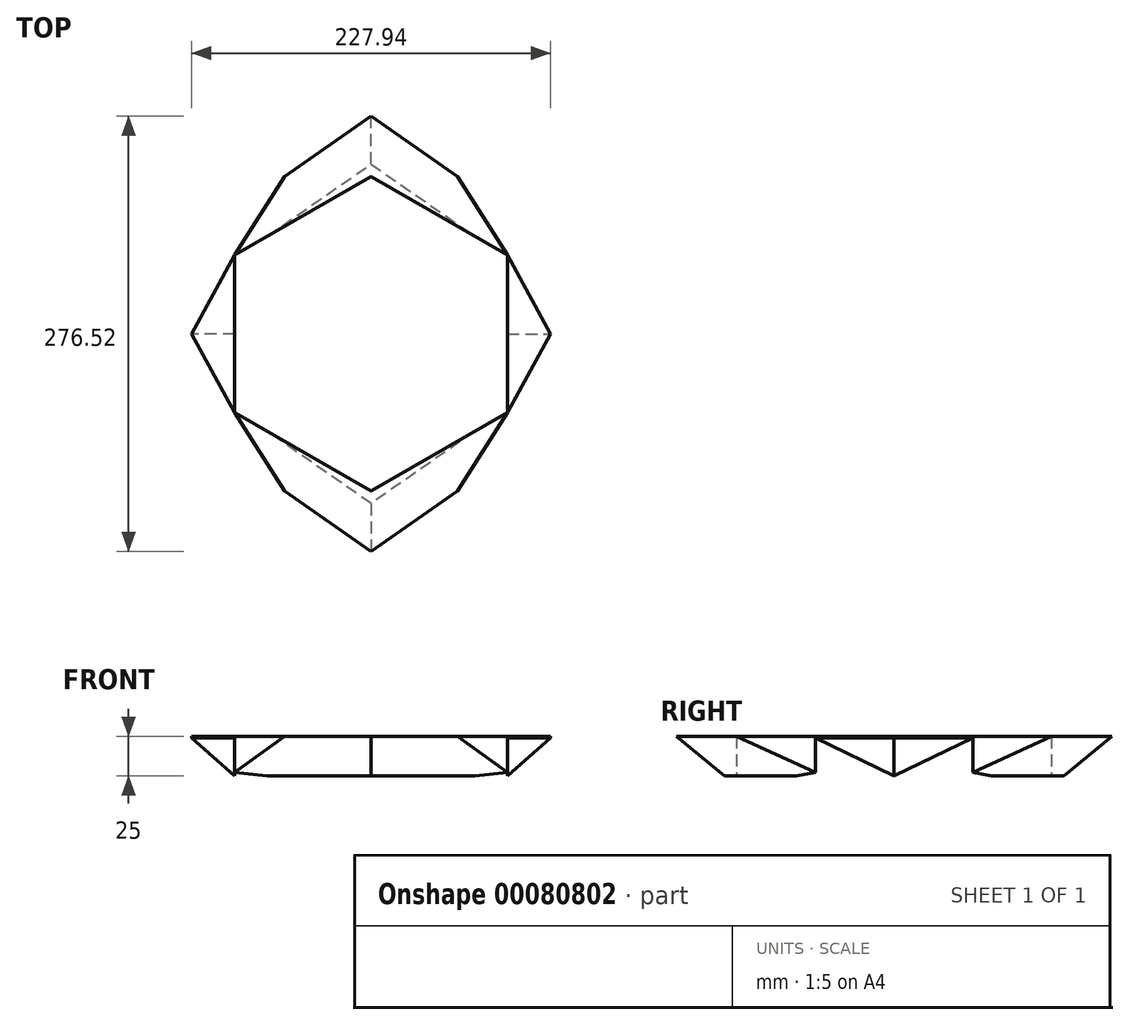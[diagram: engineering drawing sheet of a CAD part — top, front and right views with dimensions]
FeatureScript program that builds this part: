
annotation { "Feature Type Name" : "Feature", "Feature Type Description" : "" }
export const myFeature = defineFeature(function(context is Context, id is Id, definition is map)
    precondition{}
    {
        {
            var Q0;
            Q0=qCreatedBy(makeId("Top.planeOp"),FACE);
            var sketch = newSketch(context, id + "F0", { "sketchPlane" : qUnion([Q0])});
            skLineSegment(sketch, "E0.0", {"start": v(86.6, -50) * mm, "end": v(0, -100) * mm});
            skLineSegment(sketch, "E0.1", {"start": v(0, -100) * mm, "end": v(-86.6, -50) * mm});
            skLineSegment(sketch, "E0.2", {"start": v(-86.6, -50) * mm, "end": v(-86.6, 50) * mm});
            skLineSegment(sketch, "E0.3", {"start": v(-86.6, 50) * mm, "end": v(0, 100) * mm});
            skLineSegment(sketch, "E0.4", {"start": v(0, 100) * mm, "end": v(86.6, 50) * mm});
            skLineSegment(sketch, "E0.5", {"start": v(86.6, 50) * mm, "end": v(86.6, -50) * mm});
            skPoint(sketch, "E0.0.midPoint", {"position": v(43.3, -75) * mm});
            skLineSegment(sketch, "E1", {"start": v(0, 100) * mm, "end": v(-55, 100) * mm});
            skLineSegment(sketch, "E2", {"start": v(-55, 100) * mm, "end": v(-86.6, 50) * mm});
            skLineSegment(sketch, "E3", {"start": v(0, 100) * mm, "end": v(55, 100) * mm});
            skLineSegment(sketch, "E4", {"start": v(55, 100) * mm, "end": v(86.6, 50) * mm});
            skLineSegment(sketch, "E5", {"start": v(-55, 100) * mm, "end": v(0, 138.26) * mm});
            skLineSegment(sketch, "E6", {"start": v(0, 138.26) * mm, "end": v(55, 100) * mm});
            skLineSegment(sketch, "E7", {"start": v(-86.6, -50) * mm, "end": v(-113.97, 0) * mm});
            skLineSegment(sketch, "E8", {"start": v(-113.97, 0) * mm, "end": v(-86.6, 50) * mm});
            skLineSegment(sketch, "E9", {"start": v(86.6, -50) * mm, "end": v(113.97, 0) * mm});
            skLineSegment(sketch, "E10", {"start": v(113.97, 0) * mm, "end": v(86.6, 50) * mm});
            skLineSegment(sketch, "E11.MirrorCS", {"start": v(-55, -100) * mm, "end": v(-86.6, -50) * mm});
            skLineSegment(sketch, "E12.MirrorCS", {"start": v(55, -100) * mm, "end": v(86.6, -50) * mm});
            skLineSegment(sketch, "E13.MirrorCS", {"start": v(0, -100) * mm, "end": v(55, -100) * mm});
            skLineSegment(sketch, "E14.MirrorCS", {"start": v(0, -100) * mm, "end": v(-55, -100) * mm});
            skLineSegment(sketch, "E15.MirrorCS", {"start": v(0, -138.26) * mm, "end": v(55, -100) * mm});
            skLineSegment(sketch, "E16.MirrorCS", {"start": v(-55, -100) * mm, "end": v(0, -138.26) * mm});
            skSolve(sketch);
        }
        {
            var Q0;
            Q0=makeQuery(id+"F0.imprint","IMPRINT",FACE,{"disambiguationData":[TD([[makeQuery(id+"F0.imprint","IMPRINT",EDGE,{"derivedFrom":sQuery(id+"F0.wireOp",EDGE,"E0.0")}),-1.0]])]});
            var sketch = newSketch(context, id + "F1", { "sketchPlane" : qUnion([Q0])});
            skSolve(sketch);
        }
        {
            var Q0;
            Q0 = qSketchRegion(id + "F1", true);
            var Q1;
            Q1=makeQuery(id+"F1.imprint","IMPRINT",FACE,{"disambiguationData":[TD([[makeQuery(id+"F1.imprint","IMPRINT",EDGE,{"derivedFrom":makeQuery(id+"F0.imprint","IMPRINT",EDGE,{"derivedFrom":sQuery(id+"F0.wireOp",EDGE,"E0.0")})}),-1.0]])]});
            var Q2;
            Q2=makeQuery(id+"F0.imprint","IMPRINT",FACE,{"disambiguationData":[TD([[makeQuery(id+"F0.imprint","IMPRINT",EDGE,{"derivedFrom":sQuery(id+"F0.wireOp",EDGE,"E0.4")}),1.0]])]});
            var Q3;
            Q3=makeQuery(id+"F0.imprint","IMPRINT",FACE,{"disambiguationData":[TD([[makeQuery(id+"F0.imprint","IMPRINT",EDGE,{"derivedFrom":sQuery(id+"F0.wireOp",EDGE,"E0.3")}),1.0]])]});
            var Q4;
            Q4=makeQuery(id+"F0.imprint","IMPRINT",FACE,{"disambiguationData":[TD([[makeQuery(id+"F0.imprint","IMPRINT",EDGE,{"derivedFrom":sQuery(id+"F0.wireOp",EDGE,"E1")}),-1.0]])]});
            var Q5;
            Q5=makeQuery(id+"F0.imprint","IMPRINT",FACE,{"disambiguationData":[TD([[makeQuery(id+"F0.imprint","IMPRINT",EDGE,{"derivedFrom":sQuery(id+"F0.wireOp",EDGE,"E0.2")}),1.0]])]});
            var Q6;
            Q6=makeQuery(id+"F0.imprint","IMPRINT",FACE,{"disambiguationData":[TD([[makeQuery(id+"F0.imprint","IMPRINT",EDGE,{"derivedFrom":sQuery(id+"F0.wireOp",EDGE,"E0.1")}),1.0]])]});
            var Q7;
            Q7=makeQuery(id+"F0.imprint","IMPRINT",FACE,{"disambiguationData":[TD([[makeQuery(id+"F0.imprint","IMPRINT",EDGE,{"derivedFrom":sQuery(id+"F0.wireOp",EDGE,"E0.0")}),1.0]])]});
            var Q8;
            Q8=makeQuery(id+"F0.imprint","IMPRINT",FACE,{"disambiguationData":[TD([[makeQuery(id+"F0.imprint","IMPRINT",EDGE,{"derivedFrom":sQuery(id+"F0.wireOp",EDGE,"E0.5")}),1.0]])]});
            var Q9;
            Q9=makeQuery(id+"F0.imprint","IMPRINT",FACE,{"disambiguationData":[TD([[makeQuery(id+"F0.imprint","IMPRINT",EDGE,{"derivedFrom":sQuery(id+"F0.wireOp",EDGE,"E13.MirrorCS")}),-1.0]])]});
            extrude(context, id + "F2", {"entities" : qUnion([Q0, Q1, Q2, Q3, Q4, Q5, Q6, Q7, Q8, Q9]), "depth" : 25 * mm});
        }
        {
            var Q0;
            Q0=makeQuery(id+"F2.opExtrude","CAP_EDGE",EDGE,{"disambiguationData":[OSD([sQuery(id+"F0.wireOp",EDGE,"7548d645-7fa8-40ae-a30d-800e1ddf8298")])],"isStart":true});
            var Q1;
            Q1=makeQuery(id+"F2.opExtrude","CAP_EDGE",EDGE,{"disambiguationData":[OSD([sQuery(id+"F0.wireOp",EDGE,"E5")])],"isStart":true});
            var Q2;
            Q2=makeQuery(id+"F2.opExtrude","CAP_EDGE",EDGE,{"disambiguationData":[OSD([sQuery(id+"F0.wireOp",EDGE,"E6")])],"isStart":true});
            var Q3;
            Q3=makeQuery(id+"F2.opExtrude","CAP_EDGE",EDGE,{"disambiguationData":[OSD([sQuery(id+"F0.wireOp",EDGE,"E16.MirrorCS")])],"isStart":true});
            var Q4;
            Q4=makeQuery(id+"F2.opExtrude","CAP_EDGE",EDGE,{"disambiguationData":[OSD([sQuery(id+"F0.wireOp",EDGE,"E15.MirrorCS")])],"isStart":true});
            chamfer(context, id + "F3", {"entities" : qUnion([Q0, Q1, Q2, Q3, Q4]), "width" : 25 * mm, "tangentPropagation" : true});
        }
        {
            var Q0;
            Q0=makeQuery(id+"F2.opExtrude","CAP_EDGE",EDGE,{"disambiguationData":[OSD([sQuery(id+"F0.wireOp",EDGE,"8234d276-756d-4959-a82b-1161a72012dd")])],"isStart":true});
            var Q1;
            Q1=makeQuery(id+"F2.opExtrude","CAP_EDGE",EDGE,{"disambiguationData":[OSD([sQuery(id+"F0.wireOp",EDGE,"E8")])],"isStart":true});
            var Q2;
            Q2=makeQuery(id+"F2.opExtrude","CAP_EDGE",EDGE,{"disambiguationData":[OSD([sQuery(id+"F0.wireOp",EDGE,"E7")])],"isStart":true});
            var Q3;
            Q3=makeQuery(id+"F2.opExtrude","CAP_EDGE",EDGE,{"disambiguationData":[OSD([sQuery(id+"F0.wireOp",EDGE,"E9")])],"isStart":true});
            var Q4;
            Q4=makeQuery(id+"F2.opExtrude","CAP_EDGE",EDGE,{"disambiguationData":[OSD([sQuery(id+"F0.wireOp",EDGE,"E10")])],"isStart":true});
            chamfer(context, id + "F4", {"entities" : qUnion([Q0, Q1, Q2, Q3, Q4]), "width" : 24 * mm, "tangentPropagation" : true});
        }
    });
